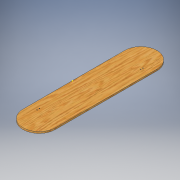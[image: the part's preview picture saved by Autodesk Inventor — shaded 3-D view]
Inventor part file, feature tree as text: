
AUTODESK INVENTOR PART (.ipt)
format: ipt  version: 2019 (Build 230136000, 136)  size: 150,016 bytes
history: native  units: mm
features: sketch x4, hole x2, other x1, extrude x1
ambient origin geometry x8: Origin, YZ Plane, XZ Plane, XY Plane, X Axis, Y Axis, Z Axis, Center Point
bodies: Body1 (feature_tree)
feature tree (8):
  other  "ソリッド1"
  sketch  "スケッチ1"
  extrude  "押し出し1"  Depth=270.0mm
  hole  "穴4"  [1 undecoded]
  hole  "穴5"  [1 undecoded]
  sketch  "スケッチ2"
  sketch  "スケッチ6"
  sketch  "スケッチ7"
note: 2 required parameter values undecoded (feature->parameter linkage not recoverable at this tier; creation-order binding heuristic only, values carry confidence <= 0.55)
